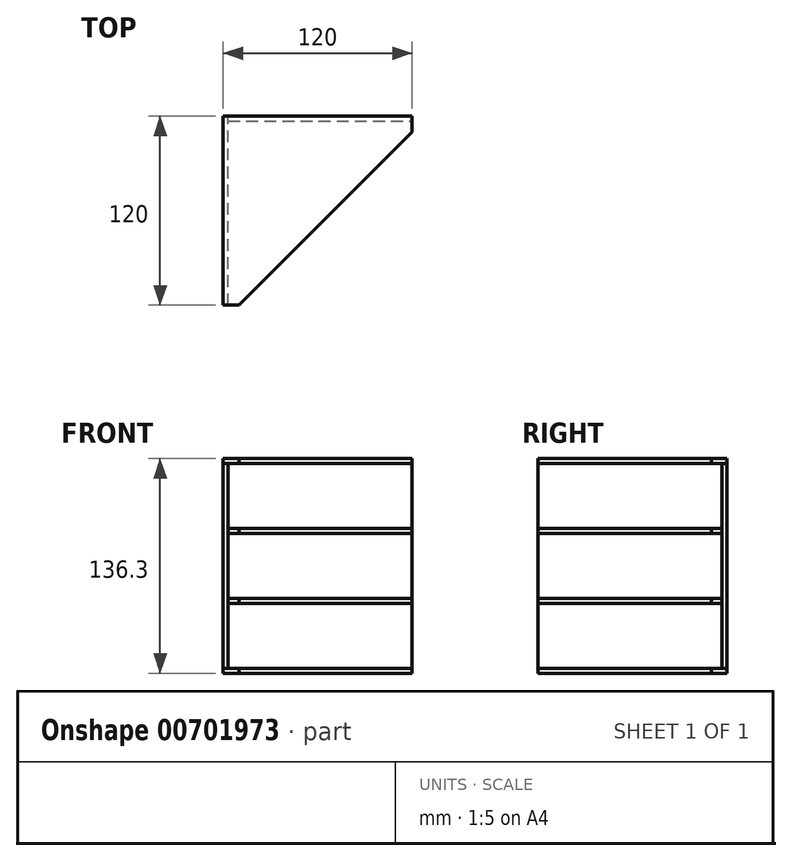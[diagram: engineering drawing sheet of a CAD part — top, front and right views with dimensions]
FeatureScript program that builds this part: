
annotation { "Feature Type Name" : "Feature", "Feature Type Description" : "" }
export const myFeature = defineFeature(function(context is Context, id is Id, definition is map)
    precondition{}
    {
        {
            assignVariable(context, id + "F0", {"name" : "x", "anyValue" : 3.15});
        }
        {
            var Q0;
            Q0=qCreatedBy(makeId("Top.planeOp"),FACE);
            var sketch = newSketch(context, id + "F1", { "sketchPlane" : qUnion([Q0])});
            skLineSegment(sketch, "E0.bottom", {"start": v(0, 0) * mm, "end": v(10, 0) * mm});
            skLineSegment(sketch, "E0.top", {"start": v(0, 120) * mm, "end": v(120, 120) * mm});
            skLineSegment(sketch, "E0.left", {"start": v(0, 0) * mm, "end": v(0, 120) * mm});
            skLineSegment(sketch, "E0.right", {"start": v(120, 110) * mm, "end": v(120, 120) * mm});
            skLineSegment(sketch, "E1", {"start": v(10, 0) * mm, "end": v(120, 110) * mm});
            skSolve(sketch);
        }
        {
            var Q0;
            Q0=qSketchRegion(id+"F1",true);
            extrude(context, id + "F2", {"entities" : qUnion([Q0]), "depth" : (getVariable(context, 'x')) * mm, "offsetDistance" : 25 * mm});
        }
        {
            var Q0;
            Q0=makeQuery(id+"F2.opExtrude","SWEPT_FACE",FACE,{"disambiguationData":[OSD([sQuery(id+"F1.wireOp",EDGE,"E0.left")])]});
            var sketch = newSketch(context, id + "F3", { "sketchPlane" : qUnion([Q0])});
            skLineSegment(sketch, "E2.top", {"start": v(0, 133.15) * mm, "end": v(-120, 133.15) * mm});
            skLineSegment(sketch, "E2.left", {"start": v(0, 3.15) * mm, "end": v(0, 133.15) * mm});
            skLineSegment(sketch, "E3", {"start": v(0, 3.15) * mm, "end": v(-120, 3.15) * mm});
            skLineSegment(sketch, "E4", {"start": v(-120, 3.15) * mm, "end": v(-120, 133.15) * mm});
            skSolve(sketch);
        }
        {
            var Q0;
            Q0=qSketchRegion(id+"F3",true);
            extrude(context, id + "F4", {"entities" : qUnion([Q0]), "oppositeDirection" : true, "depth" : (getVariable(context, 'x')) * mm, "offsetDistance" : 25 * mm});
        }
        {
            var Q0;
            Q0=makeQuery(id+"F2.opExtrude","CAP_FACE",FACE,{"disambiguationData":[OSD([sQuery(id+"F1.wireOp",EDGE,"E0.bottom"),sQuery(id+"F1.wireOp",EDGE,"E0.top"),sQuery(id+"F1.wireOp",EDGE,"E0.left"),sQuery(id+"F1.wireOp",EDGE,"E0.right"),sQuery(id+"F1.wireOp",EDGE,"E1")])],"isStart":false});
            var sketch = newSketch(context, id + "F5", { "sketchPlane" : qUnion([Q0])});
            skLineSegment(sketch, "E5.0", {"start": v(120, 110) * mm, "end": v(120, 116.85) * mm});
            skLineSegment(sketch, "E5.1", {"start": v(10, 0) * mm, "end": v(120, 110) * mm});
            skLineSegment(sketch, "E5.4", {"start": v(3.15, 0) * mm, "end": v(10, 0) * mm});
            skLineSegment(sketch, "E6", {"start": v(3.15, 0) * mm, "end": v(3.15, 116.85) * mm});
            skLineSegment(sketch, "E7", {"start": v(3.15, 116.85) * mm, "end": v(120, 116.85) * mm});
            skSolve(sketch);
        }
        {
            var Q0;
            Q0=qSketchRegion(id+"F5",true);
            extrude(context, id + "F6", {"entities" : qUnion([Q0]), "depth" : ((((130 - 2 * getVariable(context, 'x')) / 3)) + getVariable(context, 'x')) * mm, "offsetDistance" : 25 * mm, "hasSecondDirection" : true, "secondDirectionOppositeDirection" : false, "secondDirectionDepth" : ((((130 - 2 * getVariable(context, 'x')) / 3))) * mm});
        }
        {
            var Q0;
            Q0=makeQuery(id+"F2.opExtrude","SWEPT_BODY",BODY,{"disambiguationData":[OSD([sQuery(id+"F1.wireOp",EDGE,"E0.bottom"),sQuery(id+"F1.wireOp",EDGE,"E0.top"),sQuery(id+"F1.wireOp",EDGE,"E0.left"),sQuery(id+"F1.wireOp",EDGE,"E0.right")])]});
            transform(context, id + "F7", {"entities" : qUnion([Q0]), "transformType" : TransformType.TRANSLATION_3D, "dx" : 0 * mm, "dy" : 0 * mm, "dz" : 133.15 * mm, "makeCopy" : true});
        }
        {
            var Q0;
            Q0=makeQuery(id+"F7.opPattern","COPY",FACE,{"derivedFrom":makeQuery(id+"F2.opExtrude","SWEPT_FACE",FACE,{"disambiguationData":[OSD([sQuery(id+"F1.wireOp",EDGE,"E0.top")])]}),"instanceName":"1"});
            var sketch = newSketch(context, id + "F8", { "sketchPlane" : qUnion([Q0])});
            skLineSegment(sketch, "E8.bottom", {"start": v(-120, 133.15) * mm, "end": v(-3.15, 133.15) * mm});
            skLineSegment(sketch, "E8.top", {"start": v(-120, 3.15) * mm, "end": v(-3.15, 3.15) * mm});
            skLineSegment(sketch, "E8.left", {"start": v(-120, 133.15) * mm, "end": v(-120, 3.15) * mm});
            skLineSegment(sketch, "E8.right", {"start": v(-3.15, 133.15) * mm, "end": v(-3.15, 3.15) * mm});
            skSolve(sketch);
        }
        {
            var Q0;
            Q0=qSketchRegion(id+"F8",true);
            extrude(context, id + "F9", {"entities" : qUnion([Q0]), "oppositeDirection" : true, "depth" : (getVariable(context, 'x')) * mm, "offsetDistance" : 25 * mm});
        }
        {
            var Q0;
            Q0=makeQuery(id+"F6.opExtrude","SWEPT_BODY",BODY,{"disambiguationData":[OSD([sQuery(id+"F5.wireOp",EDGE,"E5.0"),sQuery(id+"F5.wireOp",EDGE,"E5.1"),sQuery(id+"F5.wireOp",EDGE,"E5.4"),sQuery(id+"F5.wireOp",EDGE,"E6"),sQuery(id+"F5.wireOp",EDGE,"E7")])]});
            transform(context, id + "F10", {"entities" : qUnion([Q0]), "transformType" : TransformType.TRANSLATION_3D, "dx" : 0 * mm, "dy" : 0 * mm, "dz" : (((((130 - 2 * getVariable(context, 'x')) / 3))) + getVariable(context, 'x')) * mm, "makeCopy" : true});
        }
    });
